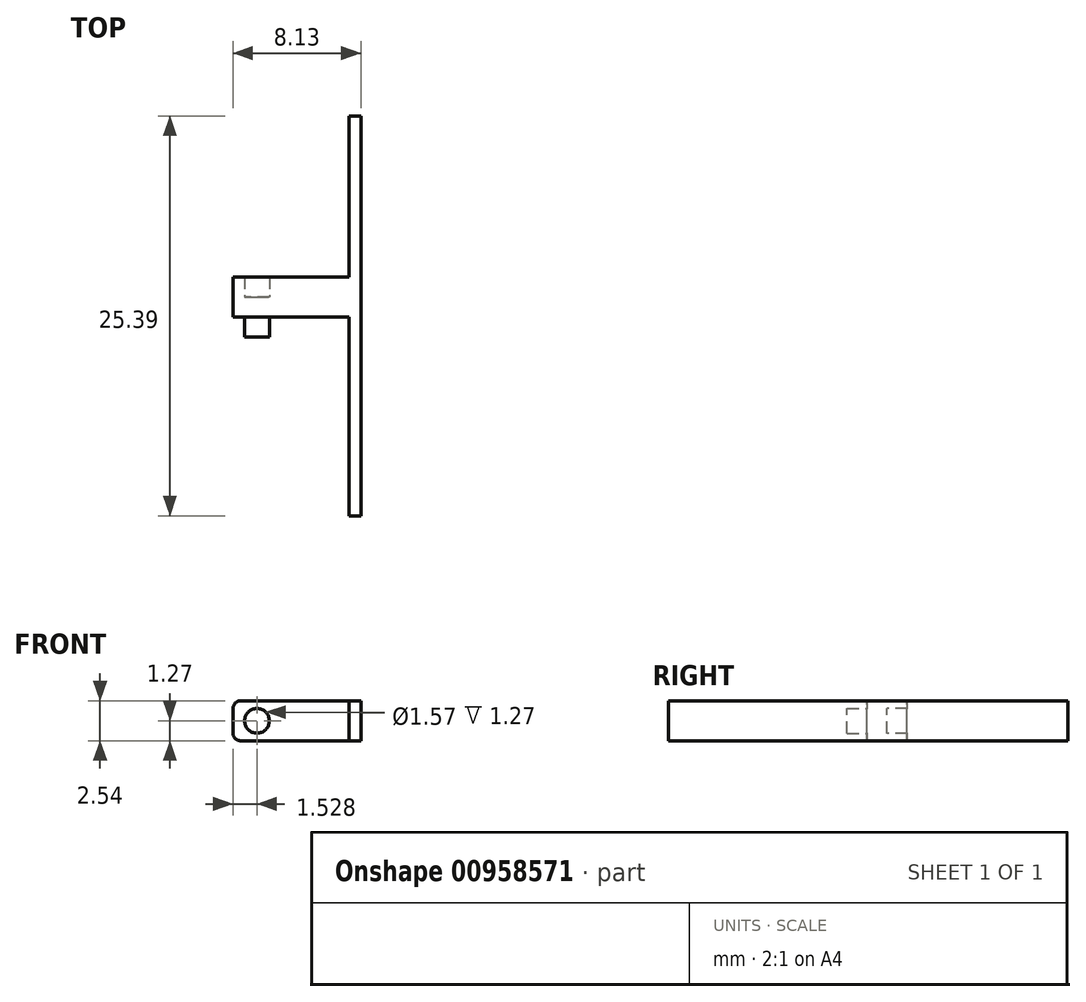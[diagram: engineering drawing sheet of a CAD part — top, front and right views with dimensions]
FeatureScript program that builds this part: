
annotation { "Feature Type Name" : "Feature", "Feature Type Description" : "" }
export const myFeature = defineFeature(function(context is Context, id is Id, definition is map)
    precondition{}
    {
        {
            var Q0;
            Q0=qCreatedBy(makeId("Front.planeOp"),FACE);
            var sketch = newSketch(context, id + "F0", { "sketchPlane" : qUnion([Q0])});
            skLineSegment(sketch, "E0.bottom", {"start": v(0.5, 0) * mm, "end": v(8.13, 0) * mm});
            skLineSegment(sketch, "E0.top", {"start": v(0.5, 2.54) * mm, "end": v(8.13, 2.54) * mm});
            skLineSegment(sketch, "E0.left", {"start": v(0, 0.5) * mm, "end": v(0, 2.03) * mm});
            skLineSegment(sketch, "E0.right", {"start": v(8.13, 0) * mm, "end": v(8.13, 2.54) * mm});
            skPoint(sketch, "E1.visualSharp", {"position": v(0, 2.54) * mm});
            skArc(sketch, "E1.filletArc", {"start": v(0.5, 2.54) * mm, "mid": v(0.15, 2.4) * mm, "end": v(0, 2.03) * mm});
            skPoint(sketch, "E2.visualSharp", {"position": v(0, 0) * mm});
            skArc(sketch, "E2.filletArc", {"start": v(0, 0.5) * mm, "mid": v(0.15, 0.15) * mm, "end": v(0.5, 0) * mm});
            skPoint(sketch, "E3", {"position": v(0, 1.27) * mm});
            skLineSegment(sketch, "E4", {"start": v(0, 1.27) * mm, "end": v(3.5, 1.27) * mm});
            skCircle(sketch, "E5", {"center": v(1.53, 1.27) * mm, "radius": 0.79 * mm});
            skSolve(sketch);
        }
        {
            var Q0;
            Q0=makeQuery(id+"F0.imprint","IMPRINT",FACE,{"disambiguationData":[TD([[makeQuery(id+"F0.imprint","IMPRINT",EDGE,{"derivedFrom":sQuery(id+"F0.wireOp",EDGE,"E0.bottom")}),1.0]])]});
            var Q1;
            {var subQ0=sQuery(id+"F0.wireOp",EDGE,"E5");var subQ1=sQuery(id+"F0.wireOp",EDGE,"E4");var subQ2=makeQuery(id+"F0.imprint","INTERSECT",VERTEX,{"disambiguationData":[OD(0.0)],"derivedFrom":[subQ1,subQ0]});Q1=makeQuery(id+"F0.imprint","IMPRINT",FACE,{"disambiguationData":[TD([[makeQuery(id+"F0.imprint","IMPRINT",EDGE,{"disambiguationData":[TD([[subQ2,-1.0]])],"derivedFrom":subQ1}),1.0]])]});}
            var Q2;
            {var subQ0=sQuery(id+"F0.wireOp",EDGE,"E5");var subQ1=sQuery(id+"F0.wireOp",EDGE,"E4");var subQ2=makeQuery(id+"F0.imprint","INTERSECT",VERTEX,{"disambiguationData":[OD(0.0)],"derivedFrom":[subQ1,subQ0]});Q2=makeQuery(id+"F0.imprint","IMPRINT",FACE,{"disambiguationData":[TD([[makeQuery(id+"F0.imprint","IMPRINT",EDGE,{"disambiguationData":[TD([[subQ2,-1.0]])],"derivedFrom":subQ1}),-1.0]])]});}
            extrude(context, id + "F1", {"entities" : qUnion([Q0, Q1, Q2]), "depth" : 2.54 * mm, "offsetDistance" : 25.4 * mm, "symmetric" : true});
        }
        {
            var Q0;
            Q0=makeQuery(id+"F1.opExtrude","SWEPT_FACE",FACE,{"disambiguationData":[OSD([sQuery(id+"F0.wireOp",EDGE,"E0.right")])]});
            var sketch = newSketch(context, id + "F2", { "sketchPlane" : qUnion([Q0])});
            skLineSegment(sketch, "E6.bottom", {"start": v(11.5, 0) * mm, "end": v(-13.9, 0) * mm});
            skLineSegment(sketch, "E6.top", {"start": v(11.5, 2.54) * mm, "end": v(-13.9, 2.54) * mm});
            skLineSegment(sketch, "E6.left", {"start": v(11.5, 0) * mm, "end": v(11.5, 2.54) * mm});
            skLineSegment(sketch, "E6.right", {"start": v(-13.9, 0) * mm, "end": v(-13.9, 2.54) * mm});
            skPoint(sketch, "E6.middle", {"position": v(-1.2, 1.27) * mm});
            skPoint(sketch, "E6.middle.positionSnap0", {"position": v(1.27, 1.27) * mm});
            skPoint(sketch, "E6.centerSnap0", {"position": v(1.27, 1.27) * mm});
            skSolve(sketch);
        }
        {
            var Q0;
            Q0 = qSketchRegion(id + "F2", true);
            extrude(context, id + "F3", {"entities" : qUnion([Q0]), "operationType" : NewBodyOperationType.ADD, "oppositeDirection" : true, "depth" : 0.76 * mm, "offsetDistance" : 25.4 * mm});
        }
        {
            var Q0;
            {var subQ0=sQuery(id+"F0.wireOp",EDGE,"E5");var subQ1=sQuery(id+"F0.wireOp",EDGE,"E4");var subQ2=makeQuery(id+"F0.imprint","INTERSECT",VERTEX,{"disambiguationData":[OD(0.0)],"derivedFrom":[subQ1,subQ0]});Q0=makeQuery(id+"F0.imprint","IMPRINT",FACE,{"disambiguationData":[TD([[makeQuery(id+"F0.imprint","IMPRINT",EDGE,{"disambiguationData":[TD([[subQ2,-1.0]])],"derivedFrom":subQ1}),1.0]])]});}
            var Q1;
            {var subQ0=sQuery(id+"F0.wireOp",EDGE,"E5");var subQ1=sQuery(id+"F0.wireOp",EDGE,"E4");var subQ2=makeQuery(id+"F0.imprint","INTERSECT",VERTEX,{"disambiguationData":[OD(0.0)],"derivedFrom":[subQ1,subQ0]});Q1=makeQuery(id+"F0.imprint","IMPRINT",FACE,{"disambiguationData":[TD([[makeQuery(id+"F0.imprint","IMPRINT",EDGE,{"disambiguationData":[TD([[subQ2,-1.0]])],"derivedFrom":subQ1}),-1.0]])]});}
            extrude(context, id + "F4", {"entities" : qUnion([Q0, Q1]), "operationType" : NewBodyOperationType.ADD, "depth" : 2.54 * mm, "offsetDistance" : 25.4 * mm});
        }
        {
            var Q0;
            {var subQ0=sQuery(id+"F0.wireOp",EDGE,"E5");var subQ1=sQuery(id+"F0.wireOp",EDGE,"E4");var subQ2=makeQuery(id+"F0.imprint","INTERSECT",VERTEX,{"disambiguationData":[OD(0.0)],"derivedFrom":[subQ1,subQ0]});Q0=makeQuery(id+"F0.imprint","IMPRINT",FACE,{"disambiguationData":[TD([[makeQuery(id+"F0.imprint","IMPRINT",EDGE,{"disambiguationData":[TD([[subQ2,-1.0]])],"derivedFrom":subQ1}),1.0]])]});}
            var Q1;
            {var subQ0=sQuery(id+"F0.wireOp",EDGE,"E5");var subQ1=sQuery(id+"F0.wireOp",EDGE,"E4");var subQ2=makeQuery(id+"F0.imprint","INTERSECT",VERTEX,{"disambiguationData":[OD(0.0)],"derivedFrom":[subQ1,subQ0]});Q1=makeQuery(id+"F0.imprint","IMPRINT",FACE,{"disambiguationData":[TD([[makeQuery(id+"F0.imprint","IMPRINT",EDGE,{"disambiguationData":[TD([[subQ2,-1.0]])],"derivedFrom":subQ1}),-1.0]])]});}
            extrude(context, id + "F5", {"entities" : qUnion([Q0, Q1]), "operationType" : NewBodyOperationType.REMOVE, "oppositeDirection" : true, "depth" : 25.4 * mm, "offsetDistance" : 25.4 * mm});
        }
    });
